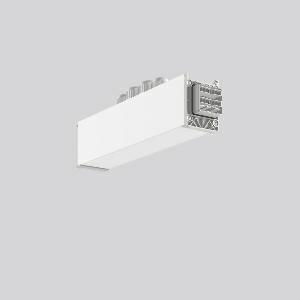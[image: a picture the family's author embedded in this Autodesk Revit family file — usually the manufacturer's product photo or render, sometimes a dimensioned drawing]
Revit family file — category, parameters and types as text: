
# Revit family: linedo_mitteleinspeisung_14pol_982698_002_8b70
name_source: partatom
category: Lighting Fixtures
units: mm (PartAtom-declared; Revit-internal decimal feet)

## family parameters
Cut with Voids When Loaded = No
Host = Face
Light Source = No
Part Type = Normal
Room Calculation Point = No
Round Connector Dimension = Use Diameter
Shared = No

## types (1)
- LINEDO_Mitteleinspeisung_14pol
    Apparent Load = 0 VA
    Default Elevation = 1800 mm
    Description = Series: LINEDO
Middle power feed, 14-pole, connection socket / plug. Housing: extruded aluminium profile, powder-coated. Cover made of plastic, surface like housing. LINEDO plug system, plastic, light grey. 4 cable glands (2 x M20 and 2 x M25). Cable glands on top. Easy connection for rigid or flexible wires.
Colour: white
Length: 330 mm
Width: 58 mm
Height: 76 mm
Weight: 850 g
    Height = 76 mm
    Lamp = 0 x
    Length = 330 mm
    Luminous efficacy = 0 lm/W
    Manufacturer = RZB
    ModVariant = No
    Model = 982698.002
    Mounting Place = Ceiling
    Mounting Type = Pendant, Surface mounted
    Number of Poles = 1
    OnlyDefault = Yes
    Power Factor = 1
    Product Name = LINEDO_Mitteleinspeisung_14pol
    Product group = Surface mounted continuous line luminaire system
    ProductGroupID = 310
    Protection Class = Protection class I
    Protection Degree = IP 54
    RLX_Detail_Level = 1
    RLX_Emergency_Light_Flux = 0 lm
    RLX_Emergency_Type = 0
    RLX_Emergency_Type_DB = No
    RlxData = <blob elided: 20637 chars, md5=6b2d9971>
    Standby Power = 0 W
    System Light Flux = 0 lm
    System Power = 0 W
    Type Comments = Product without accessories
    Type Image = 982698.002.jpg
    URL = http://relux.com
    VarID = ---
    Voltage = 0 V
    Weight = 0.00 kg
    Width = 58 mm

## geometry (parser evidence)
native form markers: Blend x4, Sweep x11
no freeform markers — native parametric forms only
